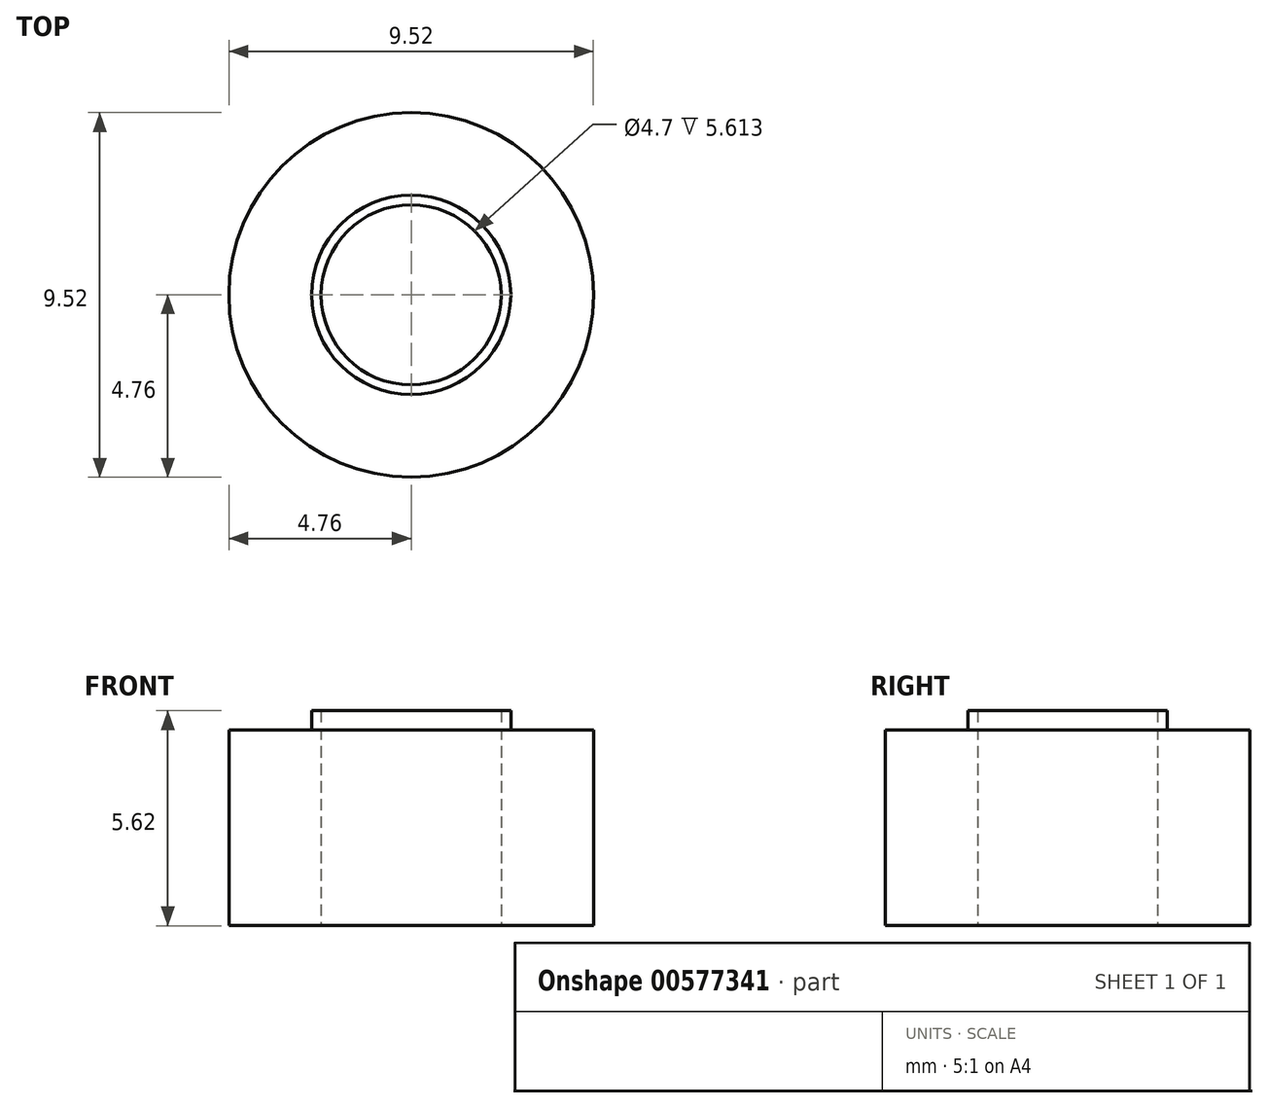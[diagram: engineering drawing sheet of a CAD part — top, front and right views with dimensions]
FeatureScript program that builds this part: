
annotation { "Feature Type Name" : "Feature", "Feature Type Description" : "" }
export const myFeature = defineFeature(function(context is Context, id is Id, definition is map)
    precondition{}
    {
        {
            var Q0;
            Q0=qCreatedBy(makeId("Top.planeOp"),FACE);
            var sketch = newSketch(context, id + "F0", { "sketchPlane" : qUnion([Q0])});
            skCircle(sketch, "E0", {"center": v(0, 0) * mm, "radius": 4.76 * mm});
            skCircle(sketch, "E1", {"center": v(0, 0) * mm, "radius": 2.35 * mm});
            skSolve(sketch);
        }
        {
            var Q0;
            Q0 = qSketchRegion(id + "F0", true);
            extrude(context, id + "F1", {"entities" : qUnion([Q0]), "endBound" : BoundingType.SYMMETRIC, "depth" : 5.61 * mm, "offsetDistance" : 25.4 * mm});
        }
        {
            var Q0;
            Q0=makeQuery(id+"F1.opExtrude","CAP_FACE",FACE,{"disambiguationData":[OSD([sQuery(id+"F0.wireOp",EDGE,"E0"),sQuery(id+"F0.wireOp",EDGE,"E1")])],"isStart":false});
            var sketch = newSketch(context, id + "F2", { "sketchPlane" : qUnion([Q0])});
            skCircle(sketch, "E2", {"center": v(0, 0) * mm, "radius": 2.6 * mm});
            skSolve(sketch);
        }
        {
            var Q0;
            Q0=makeQuery(id+"F2.imprint","IMPRINT",FACE,{"disambiguationData":[TD([[makeQuery(id+"F2.imprint","IMPRINT",EDGE,{"derivedFrom":sQuery(id+"F2.wireOp",EDGE,"E2")}),-1.0]])]});
            extrude(context, id + "F3", {"entities" : qUnion([Q0]), "operationType" : NewBodyOperationType.REMOVE, "oppositeDirection" : true, "depth" : 0.5 * mm, "offsetDistance" : 25.4 * mm});
        }
    });
